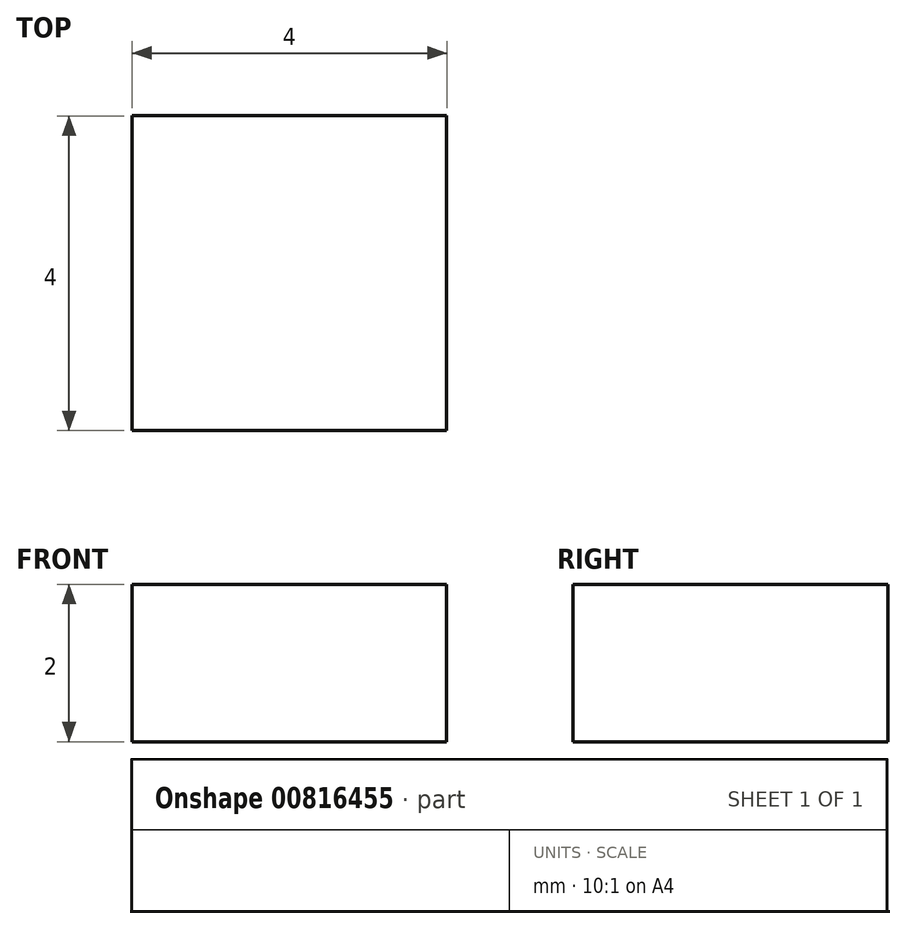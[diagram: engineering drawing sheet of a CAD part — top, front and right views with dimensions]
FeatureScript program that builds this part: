
annotation { "Feature Type Name" : "Feature", "Feature Type Description" : "" }
export const myFeature = defineFeature(function(context is Context, id is Id, definition is map)
    precondition{}
    {
        {
            var Q0;
            Q0=qCreatedBy(makeId("Top.planeOp"),FACE);
            var sketch = newSketch(context, id + "F0", { "sketchPlane" : qUnion([Q0])});
            skLineSegment(sketch, "E0.bottom", {"start": v(-3.13, 4.53) * mm, "end": v(0.87, 4.53) * mm});
            skLineSegment(sketch, "E0.top", {"start": v(-3.13, 0.53) * mm, "end": v(0.87, 0.53) * mm});
            skLineSegment(sketch, "E0.left", {"start": v(-3.13, 4.53) * mm, "end": v(-3.13, 0.53) * mm});
            skLineSegment(sketch, "E0.right", {"start": v(0.87, 4.53) * mm, "end": v(0.87, 0.53) * mm});
            skSolve(sketch);
        }
        {
            var Q0;
            Q0=makeQuery(id+"F0.imprint","IMPRINT",FACE,{"disambiguationData":[TD([[makeQuery(id+"F0.imprint","IMPRINT",EDGE,{"derivedFrom":sQuery(id+"F0.wireOp",EDGE,"E0.bottom")}),-1.0]])]});
            extrude(context, id + "F1", {"entities" : qUnion([Q0]), "depth" : 2 * mm, "offsetDistance" : 25 * mm});
        }
    });
